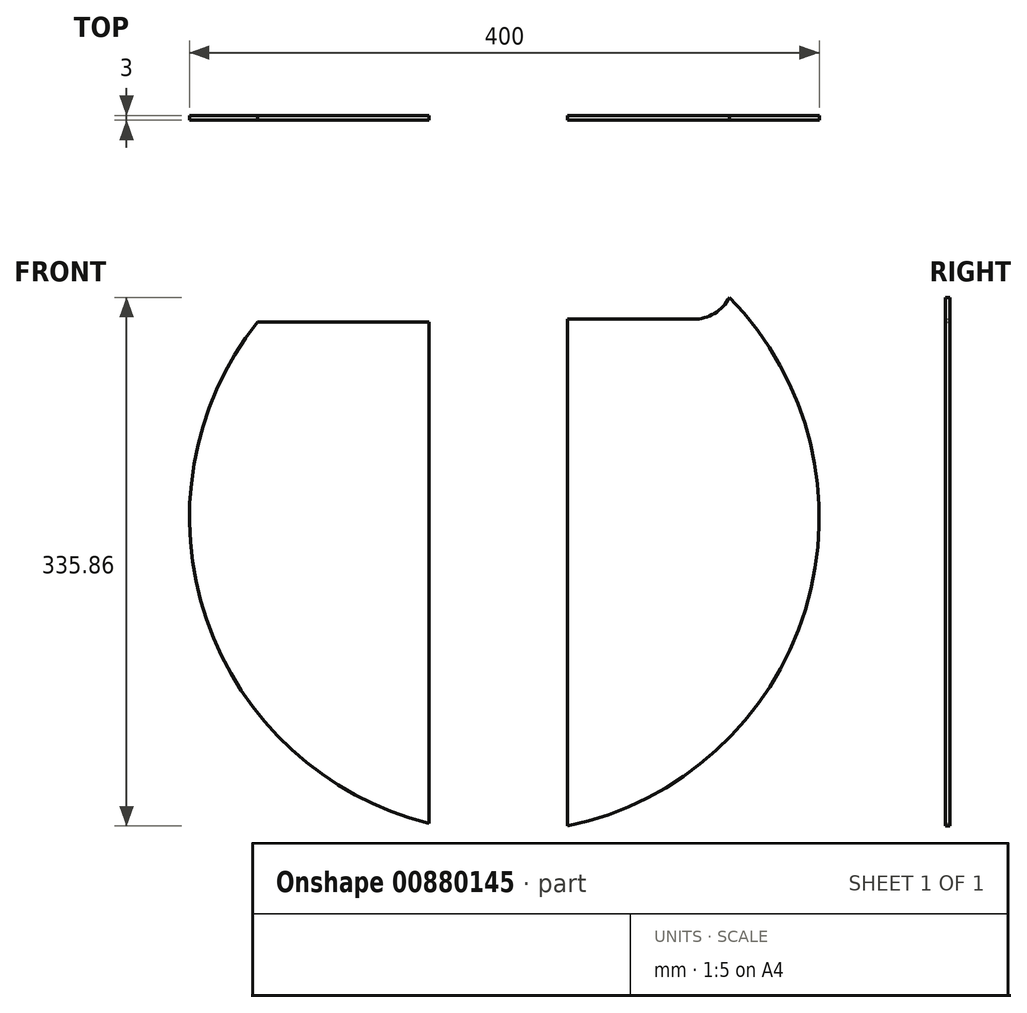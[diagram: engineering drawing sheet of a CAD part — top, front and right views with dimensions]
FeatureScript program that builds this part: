
annotation { "Feature Type Name" : "Feature", "Feature Type Description" : "" }
export const myFeature = defineFeature(function(context is Context, id is Id, definition is map)
    precondition{}
    {
        {
            var Q0;
            Q0=qCreatedBy(makeId("Front.planeOp"),FACE);
            var sketch = newSketch(context, id + "F0", { "sketchPlane" : qUnion([Q0])});
            skCircle(sketch, "E0", {"center": v(0, 0) * mm, "radius": 200 * mm});
            skLineSegment(sketch, "E1", {"start": v(0, 0) * mm, "end": v(0, 200) * mm});
            skLineSegment(sketch, "E2", {"start": v(0, 200) * mm, "end": v(0, -200) * mm});
            skLineSegment(sketch, "E3", {"start": v(0, 0) * mm, "end": v(40, 0) * mm});
            skLineSegment(sketch, "E4", {"start": v(40, 0) * mm, "end": v(40, 195.96) * mm});
            skLineSegment(sketch, "E5", {"start": v(40, 195.96) * mm, "end": v(40, -195.96) * mm});
            skLineSegment(sketch, "E6", {"start": v(40, 195.96) * mm, "end": v(40, 125.96) * mm});
            skLineSegment(sketch, "E7", {"start": v(40, 125.96) * mm, "end": v(120, 125.96) * mm});
            skArc(sketch, "E8", {"start": v(120, 125.96) * mm, "mid": v(133.42, 129.72) * mm, "end": v(142.93, 139.9) * mm});
            skLineSegment(sketch, "E9", {"start": v(0, 0) * mm, "end": v(-48, 0) * mm});
            skLineSegment(sketch, "E10", {"start": v(-48, 0) * mm, "end": v(-48, 194.15) * mm});
            skLineSegment(sketch, "E11", {"start": v(-48, 194.15) * mm, "end": v(-48, -194.15) * mm});
            skLineSegment(sketch, "E12", {"start": v(-48, 194.15) * mm, "end": v(-48, 124.15) * mm});
            skLineSegment(sketch, "E13", {"start": v(-48, 124.15) * mm, "end": v(-156.8, 124.15) * mm});
            skSolve(sketch);
        }
        {
            var Q0;
            {var subQ0=sQuery(id+"F0.wireOp",EDGE,"E5");Q0=makeQuery(id+"F0.imprint","IMPRINT",FACE,{"disambiguationData":[TD([[makeQuery(id+"F0.imprint","IMPRINT",EDGE,{"derivedFrom":subQ0}),1.0]])]});}
            extrude(context, id + "F1", {"entities" : qUnion([Q0]), "depth" : 3 * mm, "offsetDistance" : 25 * mm});
        }
        {
            var Q0;
            {var subQ0=sQuery(id+"F0.wireOp",EDGE,"E11");Q0=makeQuery(id+"F0.imprint","IMPRINT",FACE,{"disambiguationData":[TD([[makeQuery(id+"F0.imprint","IMPRINT",EDGE,{"derivedFrom":subQ0}),-1.0]])]});}
            extrude(context, id + "F2", {"entities" : qUnion([Q0]), "depth" : 3 * mm, "offsetDistance" : 25 * mm});
        }
    });
